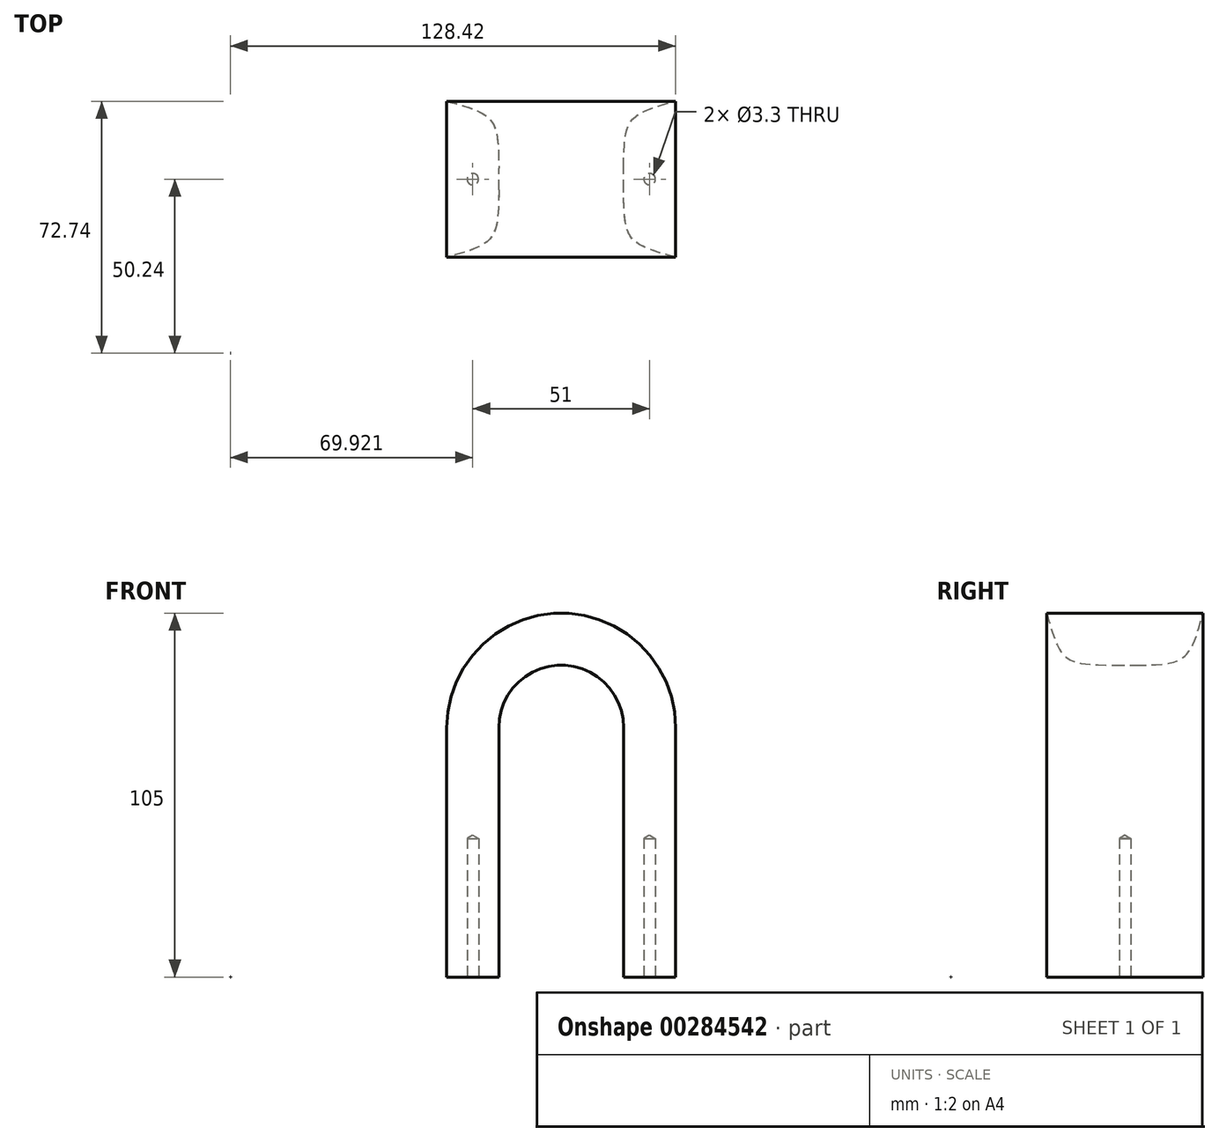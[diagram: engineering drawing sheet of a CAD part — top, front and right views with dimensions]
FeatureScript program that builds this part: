
annotation { "Feature Type Name" : "Feature", "Feature Type Description" : "" }
export const myFeature = defineFeature(function(context is Context, id is Id, definition is map)
    precondition{}
    {
        {
            var Q0;
            Q0=qCreatedBy(makeId("Top.planeOp"),FACE);
            var sketch = newSketch(context, id + "F0", { "sketchPlane" : qUnion([Q0])});
            skLineSegment(sketch, "E0.bottom", {"start": v(-87.34, -72.64) * mm, "end": v(-87.24, -72.64) * mm});
            skLineSegment(sketch, "E0.top", {"start": v(-87.34, -72.74) * mm, "end": v(-87.24, -72.74) * mm});
            skLineSegment(sketch, "E0.left", {"start": v(-87.34, -72.64) * mm, "end": v(-87.34, -72.74) * mm});
            skLineSegment(sketch, "E0.right", {"start": v(-87.24, -72.64) * mm, "end": v(-87.24, -72.74) * mm});
            skSolve(sketch);
        }
        {
            var Q0;
            Q0 = qSketchRegion(id + "F0", true);
            extrude(context, id + "F1", {"entities" : qUnion([Q0]), "depth" : 0.1 * mm});
        }
        {
            var Q0;
            Q0=qCreatedBy(makeId("Front.planeOp"),FACE);
            var sketch = newSketch(context, id + "F2", { "sketchPlane" : qUnion([Q0])});
            skArc(sketch, "E1", {"start": v(26.08, 72) * mm, "mid": v(8.08, 90) * mm, "end": v(-9.92, 72) * mm});
            skLineSegment(sketch, "E2", {"start": v(-9.92, 72) * mm, "end": v(-9.92, 0) * mm});
            skLineSegment(sketch, "E3", {"start": v(26.08, 0) * mm, "end": v(26.08, 72) * mm});
            skArc(sketch, "E4", {"start": v(41.08, 72) * mm, "mid": v(8.08, 105) * mm, "end": v(-24.92, 72) * mm});
            skLineSegment(sketch, "E5", {"start": v(-24.92, 72) * mm, "end": v(-24.92, 0) * mm});
            skLineSegment(sketch, "E6", {"start": v(-24.92, 0) * mm, "end": v(-9.92, 0) * mm});
            skLineSegment(sketch, "E7", {"start": v(41.08, 72) * mm, "end": v(41.08, 0) * mm});
            skLineSegment(sketch, "E8", {"start": v(41.08, 0) * mm, "end": v(26.08, 0) * mm});
            skSolve(sketch);
        }
        {
            var Q0;
            Q0 = qSketchRegion(id + "F2", true);
            extrude(context, id + "F3", {"entities" : qUnion([Q0]), "depth" : 45 * mm});
        }
        {
            var Q0;
            Q0=makeQuery(id+"F3.opExtrude","CAP_EDGE",EDGE,{"disambiguationData":[OSD([sQuery(id+"F2.wireOp",EDGE,"E2")])],"isStart":false});
            var Q1;
            Q1=makeQuery(id+"F3.opExtrude","CAP_EDGE",EDGE,{"disambiguationData":[OSD([sQuery(id+"F2.wireOp",EDGE,"E2")])],"isStart":true});
            fillet(context, id + "F4", {"entities" : qUnion([Q0, Q1]), "radius" : 20 * mm, "tangentPropagation" : true, "rho" : 0.7, "crossSection" : FilletCrossSection.CONIC, "allowEdgeOverflow" : false});
        }
        {
            var Q0;
            Q0=makeQuery(id+"F3.opExtrude","SWEPT_FACE",FACE,{"disambiguationData":[OSD([sQuery(id+"F2.wireOp",EDGE,"E6")])]});
            var sketch = newSketch(context, id + "F5", { "sketchPlane" : qUnion([Q0])});
            skPoint(sketch, "E9", {"position": v(-17.42, 22.5) * mm});
            skPoint(sketch, "E9.positionSnap0", {"position": v(-9.92, 22.5) * mm});
            skPoint(sketch, "E10", {"position": v(33.58, 22.5) * mm});
            skSolve(sketch);
        }
        {
            var Q0;
            Q0=sQuery(id+"F5.wireOp",VERTEX,"E9");
            var Q1;
            Q1=sQuery(id+"F5.wireOp",VERTEX,"E10");
            var Q2;
            Q2=makeQuery(id+"F3.opExtrude","SWEPT_BODY",BODY,{"disambiguationData":[OSD([sQuery(id+"F2.wireOp",EDGE,"E1"),sQuery(id+"F2.wireOp",EDGE,"E2"),sQuery(id+"F2.wireOp",EDGE,"E3"),sQuery(id+"F2.wireOp",EDGE,"E4"),sQuery(id+"F2.wireOp",EDGE,"E5"),sQuery(id+"F2.wireOp",EDGE,"E6"),sQuery(id+"F2.wireOp",EDGE,"E7"),sQuery(id+"F2.wireOp",EDGE,"E8")])]});
            hole(context, id + "F6", {"style" : HoleStyle.SIMPLE, "endStyle" : HoleEndStyle.BLIND, "holeDiameter" : 3.3 * mm, "holeDepth" : 40 * mm, "isTappedThrough" : true, "tappedDepth" : 12 * mm, "tapClearance" : 3, "locations" : qUnion([Q0, Q1]), "scope" : qUnion([Q2])});
        }
    });
